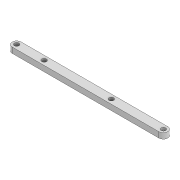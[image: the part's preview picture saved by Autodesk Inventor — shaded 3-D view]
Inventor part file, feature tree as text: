
AUTODESK INVENTOR PART (.ipt)
format: ipt  version: 2022 (Build 260153000, 153)  size: 97,280 bytes
history: native  units: mm
features: extrude x1
ambient origin geometry x8: Origin, YZ Plane, XZ Plane, XY Plane, X Axis, Y Axis, Z Axis, Center Point
bodies: Solid1 (feature_tree)
feature tree (1):
  extrude  "Extrusion1"  Depth=132.801mm
